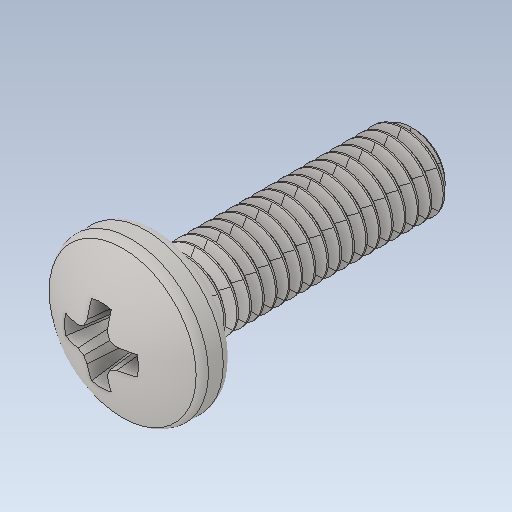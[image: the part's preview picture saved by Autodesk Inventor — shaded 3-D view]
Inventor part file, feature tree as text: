
AUTODESK INVENTOR PART (.ipt)
format: ipt  version: 2020.2 (Build 242310000, 310)  size: 1,118,720 bytes
history: imported  units: mm
features: imported_body x1
ambient origin geometry x8: Origin, YZ Plane, XZ Plane, XY Plane, X Axis, Y Axis, Z Axis, Center Point
bodies: Solide1 (imported_parasolid), Body1 (imported_parasolid)
feature tree (1):
  imported_body  NMx_Import_Brep_tag  [imported B-rep: ~6 faces, bbox_mm=None]
